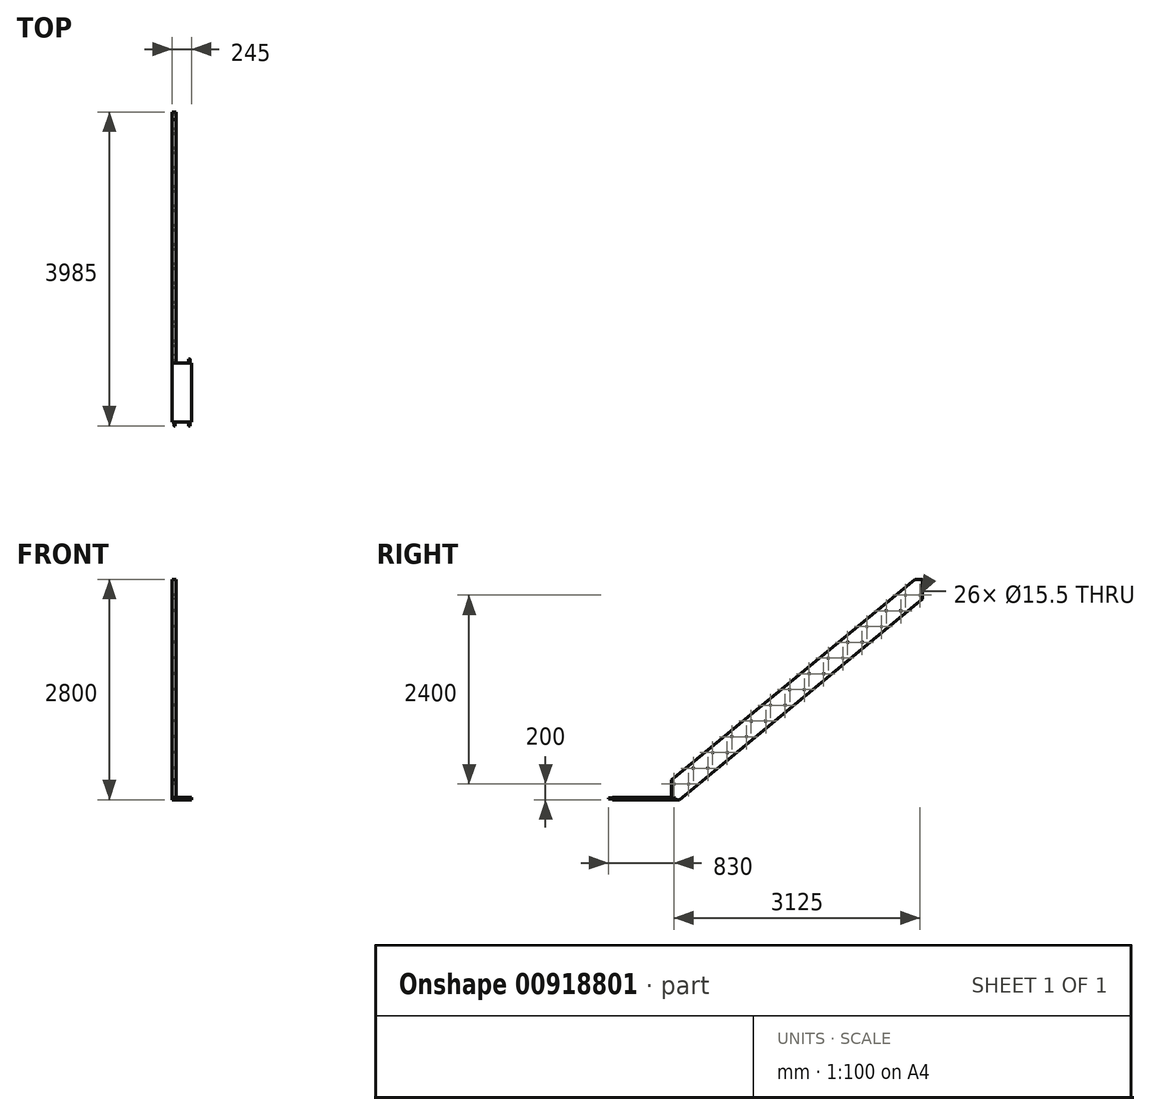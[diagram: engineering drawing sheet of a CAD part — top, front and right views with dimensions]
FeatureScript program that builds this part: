
annotation { "Feature Type Name" : "Feature", "Feature Type Description" : "" }
export const myFeature = defineFeature(function(context is Context, id is Id, definition is map)
    precondition{}
    {
        {
            var Q0;
            Q0=qCreatedBy(makeId("Right.planeOp"),FACE);
            var sketch = newSketch(context, id + "F0", { "sketchPlane" : qUnion([Q0])});
            skLineSegment(sketch, "E0", {"start": v(0, 0) * mm, "end": v(0, 200) * mm, "construction": true});
            skLineSegment(sketch, "E1", {"start": v(0, 200) * mm, "end": v(245, 200) * mm, "construction": true});
            skLineSegment(sketch, "E2", {"start": v(245, 200) * mm, "end": v(245, 400) * mm, "construction": true});
            skLineSegment(sketch, "E3", {"start": v(245, 400) * mm, "end": v(490, 400) * mm, "construction": true});
            skLineSegment(sketch, "E4", {"start": v(490, 400) * mm, "end": v(490, 600) * mm, "construction": true});
            skLineSegment(sketch, "E5", {"start": v(490, 600) * mm, "end": v(735, 600) * mm, "construction": true});
            skLineSegment(sketch, "E6", {"start": v(735, 600) * mm, "end": v(735, 800) * mm, "construction": true});
            skLineSegment(sketch, "E7", {"start": v(735, 800) * mm, "end": v(980, 800) * mm, "construction": true});
            skLineSegment(sketch, "E8", {"start": v(980, 800) * mm, "end": v(980, 1000) * mm, "construction": true});
            skLineSegment(sketch, "E9", {"start": v(980, 1000) * mm, "end": v(1225, 1000) * mm, "construction": true});
            skLineSegment(sketch, "E10", {"start": v(1225, 1000) * mm, "end": v(1225, 1200) * mm, "construction": true});
            skLineSegment(sketch, "E11", {"start": v(1225, 1200) * mm, "end": v(1470, 1200) * mm, "construction": true});
            skLineSegment(sketch, "E12", {"start": v(1470, 1200) * mm, "end": v(1470, 1400) * mm, "construction": true});
            skLineSegment(sketch, "E13", {"start": v(1470, 1400) * mm, "end": v(1715, 1400) * mm, "construction": true});
            skLineSegment(sketch, "E14", {"start": v(1715, 1400) * mm, "end": v(1715, 1600) * mm, "construction": true});
            skLineSegment(sketch, "E15", {"start": v(1715, 1600) * mm, "end": v(1960, 1600) * mm, "construction": true});
            skLineSegment(sketch, "E16", {"start": v(1960, 1600) * mm, "end": v(1960, 1800) * mm, "construction": true});
            skLineSegment(sketch, "E17", {"start": v(1960, 1800) * mm, "end": v(2205, 1800) * mm, "construction": true});
            skLineSegment(sketch, "E18", {"start": v(2205, 1800) * mm, "end": v(2205, 2000) * mm, "construction": true});
            skLineSegment(sketch, "E19", {"start": v(2205, 2000) * mm, "end": v(2450, 2000) * mm, "construction": true});
            skLineSegment(sketch, "E20", {"start": v(2450, 2000) * mm, "end": v(2450, 2200) * mm, "construction": true});
            skLineSegment(sketch, "E21", {"start": v(2450, 2200) * mm, "end": v(2695, 2200) * mm, "construction": true});
            skLineSegment(sketch, "E22", {"start": v(2695, 2200) * mm, "end": v(2695, 2400) * mm, "construction": true});
            skLineSegment(sketch, "E23", {"start": v(2695, 2400) * mm, "end": v(2940, 2400) * mm, "construction": true});
            skLineSegment(sketch, "E24", {"start": v(2940, 2400) * mm, "end": v(2940, 2600) * mm, "construction": true});
            skLineSegment(sketch, "E25", {"start": v(2940, 2600) * mm, "end": v(3185, 2600) * mm, "construction": true});
            skLineSegment(sketch, "E26", {"start": v(3185, 2600) * mm, "end": v(3185, 2800) * mm, "construction": true});
            skLineSegment(sketch, "E27", {"start": v(3185, 2800) * mm, "end": v(3430, 2800) * mm, "construction": true});
            skLineSegment(sketch, "E28", {"start": v(100, 0) * mm, "end": v(3430, 2750) * mm});
            skLineSegment(sketch, "E29", {"start": v(3330, 3000) * mm, "end": v(0, 250) * mm});
            skLineSegment(sketch, "E30", {"start": v(0, 250) * mm, "end": v(0, 0) * mm});
            skLineSegment(sketch, "E31", {"start": v(100, 0) * mm, "end": v(0, 0) * mm});
            skLineSegment(sketch, "E32", {"start": v(3430, 2800) * mm, "end": v(3430, 3000) * mm, "construction": true});
            skLineSegment(sketch, "E33", {"start": v(3330, 3000) * mm, "end": v(3430, 3000) * mm});
            skLineSegment(sketch, "E34", {"start": v(3430, 3000) * mm, "end": v(3430, 2750) * mm});
            skPoint(sketch, "E35", {"position": v(30, 200) * mm});
            skPoint(sketch, "E36", {"position": v(3400, 2800) * mm});
            skPoint(sketch, "E37", {"position": v(215, 200) * mm});
            skPoint(sketch, "E38", {"position": v(275, 400) * mm});
            skPoint(sketch, "E39", {"position": v(460, 400) * mm});
            skPoint(sketch, "E40", {"position": v(520, 600) * mm});
            skPoint(sketch, "E41", {"position": v(705, 600) * mm});
            skPoint(sketch, "E42", {"position": v(765, 800) * mm});
            skPoint(sketch, "E43", {"position": v(950, 800) * mm});
            skPoint(sketch, "E44", {"position": v(1010, 1000) * mm});
            skPoint(sketch, "E45", {"position": v(1195, 1000) * mm});
            skPoint(sketch, "E46", {"position": v(1255, 1200) * mm});
            skPoint(sketch, "E47", {"position": v(1440, 1200) * mm});
            skPoint(sketch, "E48", {"position": v(1500, 1400) * mm});
            skPoint(sketch, "E49", {"position": v(1685, 1400) * mm});
            skPoint(sketch, "E50", {"position": v(1745, 1600) * mm});
            skPoint(sketch, "E51", {"position": v(1930, 1600) * mm});
            skPoint(sketch, "E52", {"position": v(1990, 1800) * mm});
            skPoint(sketch, "E53", {"position": v(2175, 1800) * mm});
            skPoint(sketch, "E54", {"position": v(2235, 2000) * mm});
            skPoint(sketch, "E55", {"position": v(2420, 2000) * mm});
            skPoint(sketch, "E56", {"position": v(2480, 2200) * mm});
            skPoint(sketch, "E57", {"position": v(2665, 2200) * mm});
            skPoint(sketch, "E58", {"position": v(2725, 2400) * mm});
            skPoint(sketch, "E59", {"position": v(2910, 2400) * mm});
            skPoint(sketch, "E60", {"position": v(2970, 2600) * mm});
            skPoint(sketch, "E61", {"position": v(3155, 2600) * mm});
            skPoint(sketch, "E62", {"position": v(3215, 2800) * mm});
            skLineSegment(sketch, "E63", {"start": v(3087.82, 2800) * mm, "end": v(3185, 2800) * mm});
            skLineSegment(sketch, "E64", {"start": v(3185, 2547.67) * mm, "end": v(3185, 2800) * mm});
            skSolve(sketch);
        }
        {
            var Q0;
            {var subQ0=sQuery(id+"F0.wireOp",EDGE,"E30");Q0=makeQuery(id+"F0.imprint","IMPRINT",FACE,{"disambiguationData":[TD([[makeQuery(id+"F0.imprint","IMPRINT",EDGE,{"derivedFrom":subQ0}),1.0]])]});}
            extrude(context, id + "F1", {"entities" : qUnion([Q0]), "depth" : 50 * mm, "offsetDistance" : 25 * mm});
        }
        {
            var Q0;
            Q0=sQuery(id+"F0.wireOp",VERTEX,"E36");
            var Q1;
            Q1=sQuery(id+"F0.wireOp",VERTEX,"E35");
            var Q2;
            Q2=sQuery(id+"F0.wireOp",VERTEX,"E37");
            var Q3;
            Q3=sQuery(id+"F0.wireOp",VERTEX,"E38");
            var Q4;
            Q4=sQuery(id+"F0.wireOp",VERTEX,"E39");
            var Q5;
            Q5=sQuery(id+"F0.wireOp",VERTEX,"E40");
            var Q6;
            Q6=sQuery(id+"F0.wireOp",VERTEX,"E41");
            var Q7;
            Q7=sQuery(id+"F0.wireOp",VERTEX,"E42");
            var Q8;
            Q8=sQuery(id+"F0.wireOp",VERTEX,"E43");
            var Q9;
            Q9=sQuery(id+"F0.wireOp",VERTEX,"E44");
            var Q10;
            Q10=sQuery(id+"F0.wireOp",VERTEX,"E45");
            var Q11;
            Q11=sQuery(id+"F0.wireOp",VERTEX,"E46");
            var Q12;
            Q12=sQuery(id+"F0.wireOp",VERTEX,"E47");
            var Q13;
            Q13=sQuery(id+"F0.wireOp",VERTEX,"E48");
            var Q14;
            Q14=sQuery(id+"F0.wireOp",VERTEX,"E49");
            var Q15;
            Q15=sQuery(id+"F0.wireOp",VERTEX,"E50");
            var Q16;
            Q16=sQuery(id+"F0.wireOp",VERTEX,"E51");
            var Q17;
            Q17=sQuery(id+"F0.wireOp",VERTEX,"E52");
            var Q18;
            Q18=sQuery(id+"F0.wireOp",VERTEX,"E53");
            var Q19;
            Q19=sQuery(id+"F0.wireOp",VERTEX,"E54");
            var Q20;
            Q20=sQuery(id+"F0.wireOp",VERTEX,"E55");
            var Q21;
            Q21=sQuery(id+"F0.wireOp",VERTEX,"E56");
            var Q22;
            Q22=sQuery(id+"F0.wireOp",VERTEX,"E57");
            var Q23;
            Q23=sQuery(id+"F0.wireOp",VERTEX,"E58");
            var Q24;
            Q24=sQuery(id+"F0.wireOp",VERTEX,"E59");
            var Q25;
            Q25=sQuery(id+"F0.wireOp",VERTEX,"E60");
            var Q26;
            Q26=sQuery(id+"F0.wireOp",VERTEX,"E61");
            var Q27;
            Q27=sQuery(id+"F0.wireOp",VERTEX,"E62");
            var Q28;
            Q28=makeQuery(id+"F1.opExtrude","SWEPT_BODY",BODY,{"disambiguationData":[OSD([sQuery(id+"F0.wireOp",EDGE,"E28"),sQuery(id+"F0.wireOp",EDGE,"E29"),sQuery(id+"F0.wireOp",EDGE,"E30"),sQuery(id+"F0.wireOp",EDGE,"E31"),sQuery(id+"F0.wireOp",EDGE,"E33"),sQuery(id+"F0.wireOp",EDGE,"E34")])]});
            hole(context, id + "F2", {"style" : HoleStyle.SIMPLE, "endStyle" : HoleEndStyle.THROUGH, "oppositeDirection" : true, "standardTappedOrClearance" : lookupTablePath({ "fit" : "Normal", "standard" : "ISO", "size" : "M14", "type" : "Clearance" }), "standardBlindInLast" : lookupTablePath({ "fit" : "Normal", "standard" : "ISO", "size" : "M14", "type" : "Clearance" }), "holeDiameter" : 15.5 * mm, "majorDiameter" : 5 * mm, "isTappedThrough" : true, "tappedDepth" : 12 * mm, "tapClearance" : 3, "locations" : qUnion([Q0, Q1, Q2, Q3, Q4, Q5, Q6, Q7, Q8, Q9, Q10, Q11, Q12, Q13, Q14, Q15, Q16, Q17, Q18, Q19, Q20, Q21, Q22, Q23, Q24, Q25, Q26, Q27]), "scope" : qUnion([Q28])});
        }
        {
            var Q0;
            Q0=qCreatedBy(makeId("Front.planeOp"),FACE);
            var sketch = newSketch(context, id + "F3", { "sketchPlane" : qUnion([Q0])});
            skLineSegment(sketch, "E65.bottom", {"start": v(0, 0) * mm, "end": v(245, 0) * mm});
            skLineSegment(sketch, "E65.top", {"start": v(0, 30) * mm, "end": v(245, 30) * mm});
            skLineSegment(sketch, "E65.left", {"start": v(0, 0) * mm, "end": v(0, 30) * mm});
            skLineSegment(sketch, "E65.right", {"start": v(245, 0) * mm, "end": v(245, 30) * mm});
            skSolve(sketch);
        }
        {
            var Q0;
            Q0=makeQuery(id+"F3.imprint","IMPRINT",FACE,{"disambiguationData":[TD([[makeQuery(id+"F3.imprint","IMPRINT",EDGE,{"derivedFrom":sQuery(id+"F3.wireOp",EDGE,"E65.bottom")}),1.0]])]});
            extrude(context, id + "F4", {"entities" : qUnion([Q0]), "depth" : 750 * mm, "offsetDistance" : 25 * mm});
        }
        {
            var Q0;
            Q0=makeQuery(id+"F4.opExtrude","CAP_FACE",FACE,{"disambiguationData":[OSD([sQuery(id+"F3.wireOp",EDGE,"E65.bottom"),sQuery(id+"F3.wireOp",EDGE,"E65.top"),sQuery(id+"F3.wireOp",EDGE,"E65.left"),sQuery(id+"F3.wireOp",EDGE,"E65.right")])],"isStart":false});
            var sketch = newSketch(context, id + "F5", { "sketchPlane" : qUnion([Q0])});
            skCircle(sketch, "E66", {"center": v(30, 15) * mm, "radius": 7.5 * mm});
            skPoint(sketch, "E66.centerSnap0", {"position": v(0, 15) * mm});
            skCircle(sketch, "E67", {"center": v(215, 15) * mm, "radius": 7.5 * mm});
            skPoint(sketch, "E67.centerSnap0", {"position": v(245, 15) * mm});
            skSolve(sketch);
        }
        {
            var Q0;
            Q0=makeQuery(id+"F5.imprint","IMPRINT",FACE,{"disambiguationData":[TD([[makeQuery(id+"F5.imprint","IMPRINT",EDGE,{"derivedFrom":sQuery(id+"F5.wireOp",EDGE,"E66")}),1.0]])]});
            var Q1;
            Q1=makeQuery(id+"F5.imprint","IMPRINT",FACE,{"disambiguationData":[TD([[makeQuery(id+"F5.imprint","IMPRINT",EDGE,{"derivedFrom":sQuery(id+"F5.wireOp",EDGE,"E67")}),1.0]])]});
            extrude(context, id + "F6", {"entities" : qUnion([Q0, Q1]), "operationType" : NewBodyOperationType.ADD, "depth" : 50 * mm, "offsetDistance" : 25 * mm, "hasSecondDirection" : true, "secondDirectionOppositeDirection" : true, "secondDirectionDepth" : (750 + 50) * mm});
        }
    });
